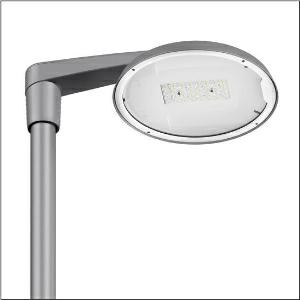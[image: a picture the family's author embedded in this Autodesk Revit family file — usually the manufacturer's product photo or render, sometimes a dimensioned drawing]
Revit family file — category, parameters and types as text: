
# Revit family: dl_50_iq_mini___st0_5a_5xa248b41f08je_5338
name_source: partatom
category: Lighting Fixtures
units: mm (PartAtom-declared; Revit-internal decimal feet)

## family parameters
Cut with Voids When Loaded = No
Host = Face
Light Source = No
Part Type = Normal
Room Calculation Point = No
Round Connector Dimension = Use Diameter
Shared = No

## types (1)
- --- (1 x LED, 10300 lm, 62.6 W, 4000K)
    Apparent Load = 63 VA
    CIE Flux Codes = 43 76 97 100 100
    Color Rendering = 70
    Color Temperature = 4000K
    Default Elevation = 1800 mm
    Description = DL 50 iQ mini, mast luminaire, primary light control with lens, of PMMA, primary optical cover: cover, of toughened safety glass, transparent, light distribution: ST0.5a, light emission: direct distribution, primary light characteristic: asymmetric, installation type: side-entry, post-top, LED, High Power LED, rated luminous flux: 10.300lm, luminous efficacy: 165lm/W, light colour: 740, colour temperature: 4000K, control gear: iQ Street-Remote, control: optimised constant luminous flux control (CLO 2.0), Desk-Remote (wireless, voltage-free reading and setting of iQ features in the workshop via application-optimized NFC function/RFID function), Light-Fading, Smart-Wire, Night-Set, Lumen-Switch, Temp-Guard, Auto-Match, Street-Remote, mains connection: 230..240V, AC, 50/60Hz, connection cable pre-assembled, cable length: 8,5m, start of lifetime: 63W, end of service life: 65W, reduction: 29W, luminaire housing, of diecast aluminium, powder-coated, SITECO metallic grey (DB 702S), inclination adjustable: 0°, 5°, 10° (post-top) | 0°, -5°, -10°, -15° (side-entry), please order mast post-top element or mast side-entry element separately, diameter: 500mm, height: 115mm, post-top: for spigot size d x l = 76 x 100mm; with reducer (optional accessory) 60 x 100mm | side-entry: for spigot size d x l = 60 x 100mm; with reducer (optional accessory) 42 x 100mm, mounting height: 4..6m, protection rating (complete): IP66, insulation class (complete): insulation class II (safety insulation), certification: CE, ENEC, ENEC+, VDE, impact resistance: IK08, permissible operating ambient temperature for outdoor applications: -25..+40°C, standard-compliant lighting for roads and squares, packaging unit: 1 piece

Light Distribution: ST0.5a
    Height = 115 mm
    Lamp = 1 x LED
    Lamp Light Flux = 10300 lm
    Lamp Power = 62.6 W
    Lamp count = 1
    Length = 500 mm
    Luminous efficacy = 165 lm/W
    Manufacturer = Siteco
    ModVariant = No
    Model = 5XA248B41F08JE
    Mounting Place = Pole
    Mounting Type = Pole top
    Number of Poles = 1
    OnlyDefault = Yes
    Power Factor = 1
    Product Name = DL 50 iQ mini | ST0.5a
    Product group = mast luminaire | pylon top
    ProductGroupID = 6100
    Protection Class = Protection class II
    Protection Degree = IP 66
    RLX_Detail_Level = 1
    RLX_Emergency_Light_Flux = 0 lm
    RLX_Emergency_Type = 0
    RLX_Emergency_Type_DB = No
    RlxData = <blob elided: 127041 chars, md5=dc8830f1>
    Socket = socket
    Standby Power = 0 W
    System Light Flux = 10300 lm
    System Power = 63 W
    Type Comments = factory setting: luminous flux: 100 % | dim-lin: 254 | 658 mA
    Type Image = l_1251794.jpg
    URL = http://relux.com
    VarID = @adj_143933
    Voltage = 0 V
    Weight = 0.00 kg
    Width = 0 mm  [stored 0 ft]

note: [stored X ft] marks values corroborated as IEEE doubles in the binary element streams (Revit-internal decimal feet)

## geometry (parser evidence)
native form markers: Blend x4, Sweep x10
no freeform markers — native parametric forms only
